# Revit family: Gira_0214426
name_source: partatom
category: Electrical Fixtures
revit_build: Autodesk Revit 2017 (Build: 20160225_1515(x64)
units: mm (PartAtom-declared; Revit-internal decimal feet)

## family parameters
Cut with Voids When Loaded = No
Host = Face
Maintain Annotation Orientation = No
Part Type = Normal
Room Calculation Point = No
Round Connector Dimension = Use Diameter
Shared = No

## types (1)
- Cov.fr. 4-g Gira E3 umber/anthra.
    Available = No
    BIM (1) = https://media.stage.bim.site
    Category = Cover frame for domestic switching devices
    Data sheet (1) = https://katalog.gira.de
    Default Elevation = 1219 mm
    Description = Cov.fr.4g E3 UmAn,Gira E3 cover frame,umber soft touch with anthracite intermediate frame,4-gang,Features:,- Shatter-proof.,,Notes :,- Soft-touch surface,- NCS value: approx. NCS S 7010-Y10R
    GTIN = 4010337024484
    HAN = 0214426
    HeinzeBIM = https://bimportal.heinze.de
    Manufacturer = Gira
    Manufacturer URL = https://www.gira.de
    Name = Cov.fr. 4-g Gira E3 umber/anthra.
    Transparent = No
    URL = http://katalog.gira.de

## geometry (parser evidence)
native form markers: Blend x2, Sweep x3
no freeform markers — native parametric forms only
